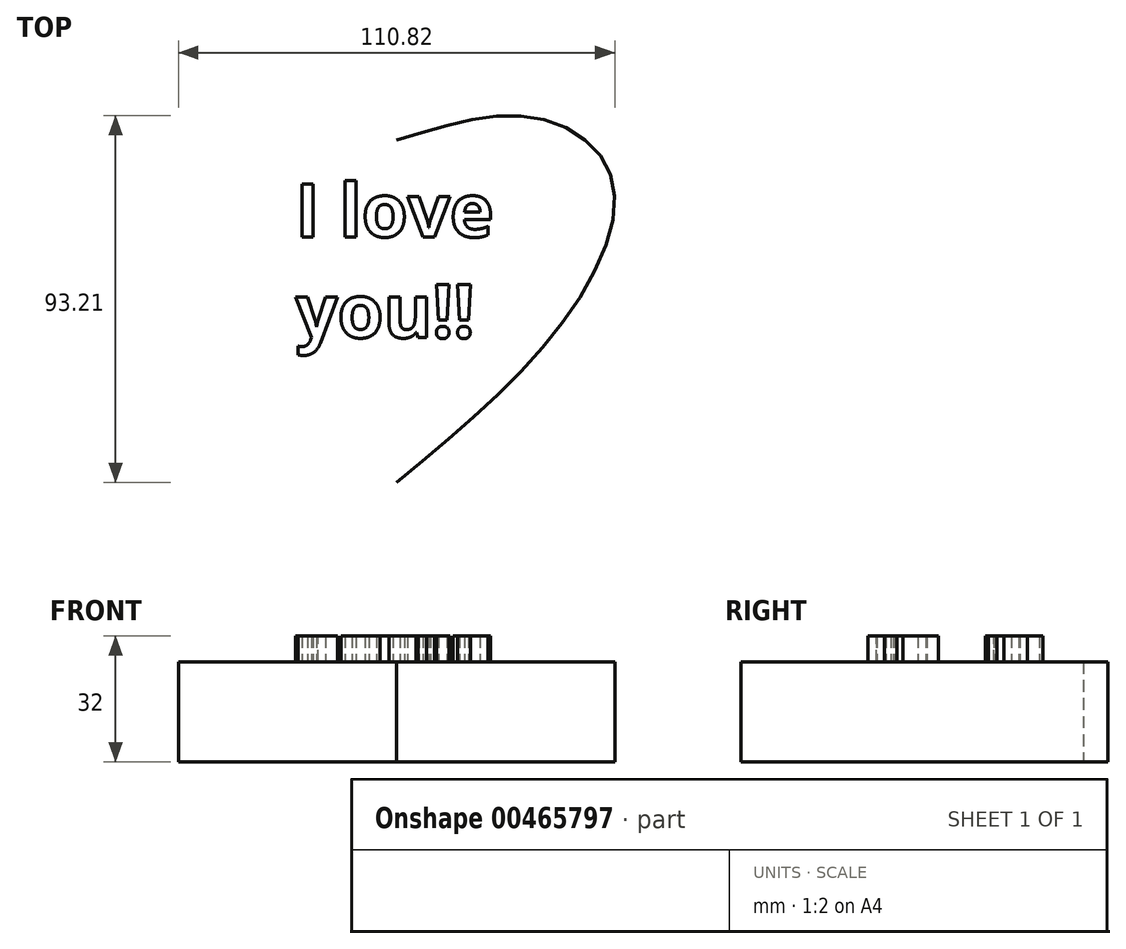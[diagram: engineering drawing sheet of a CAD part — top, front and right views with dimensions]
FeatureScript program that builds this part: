
annotation { "Feature Type Name" : "Feature", "Feature Type Description" : "" }
export const myFeature = defineFeature(function(context is Context, id is Id, definition is map)
    precondition{}
    {
        {
            var Q0;
            Q0=qCreatedBy(makeId("Top.planeOp"),FACE);
            var sketch = newSketch(context, id + "F0", { "sketchPlane" : qUnion([Q0])});
            skFitSpline(sketch, "E0", {"points": [v(0, 52.33) * mm, v(34.22, 58.12) * mm, v(54.6, 42.77) * mm, v(42.77, 6.8) * mm, v(0, -34.72) * mm], "startDerivative": vector(148.35, 41.08) * mm, "endDerivative": vector(-152.24, -125.78) * mm});
            skFitSpline(sketch, "E1.MirrorCS", {"points": [v(0, 52.33) * mm, v(-34.22, 58.12) * mm, v(-54.6, 42.77) * mm, v(-42.77, 6.8) * mm, v(0, -34.72) * mm], "startDerivative": vector(-148.35, 41.08) * mm, "endDerivative": vector(152.24, -125.78) * mm});
            skSolve(sketch);
        }
        {
            var Q0;
            Q0 = qSketchRegion(id + "F0", true);
            extrude(context, id + "F1", {"entities" : qUnion([Q0]), "depth" : 25.4 * mm});
        }
        {
            var Q0;
            Q0=makeQuery(id+"F1.opExtrude","CAP_FACE",FACE,{"disambiguationData":[OSD([sQuery(id+"F0.wireOp",EDGE,"E0"),sQuery(id+"F0.wireOp",EDGE,"E1.MirrorCS")])],"isStart":false});
            var sketch = newSketch(context, id + "F2", { "sketchPlane" : qUnion([Q0])});
            skText(sketch, "E2", { "text": "I love \nyou!!\n", "fontName": "OpenSans-Bold.ttf"});
            const initialGuessF2  = {"E2": [-0.02574, 0.02768, 1, 0, 0.01356]};
            skSetInitialGuess(sketch, initialGuessF2);
            skSolve(sketch);
        }
        {
            var Q0;
            Q0 = qSketchRegion(id + "F2", true);
            extrude(context, id + "F3", {"entities" : qUnion([Q0]), "operationType" : NewBodyOperationType.ADD, "depth" : 6.6 * mm});
        }
    });
